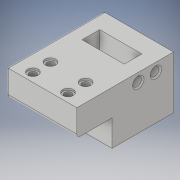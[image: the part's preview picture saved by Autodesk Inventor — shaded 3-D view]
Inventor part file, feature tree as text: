
AUTODESK INVENTOR PART (.ipt)
format: ipt  version: 2019 (Build 230136000, 136)  size: 223,744 bytes
history: native  units: mm
features: sketch x10, extrude x5, hole x5, fillet x2, mirror x1
ambient origin geometry x8: Origin, YZ Plane, XZ Plane, XY Plane, X Axis, Y Axis, Z Axis, Center Point
bodies: Solid1 (feature_tree)
feature tree (23):
  extrude  "Extrusion1"  Depth=20.0mm
  hole  "Hole1"  [1 undecoded]
  fillet  "Fillet1"  Radius=2.0mm
  extrude  "Extrusion2"  Depth=30.0mm
  extrude  "Extrusion3"  Depth=10.0mm TaperAngle=0.0deg
  hole  "Hole2"  [1 undecoded]
  hole  "Hole3"  [1 undecoded]
  extrude  "Extrusion4"  Depth=10.0mm
  extrude  "Extrusion5"  Depth=20.0mm
  hole  "Hole4"  [1 undecoded]
  hole  "Hole5"  [1 undecoded]
  mirror  "Mirror1"
  fillet  "Fillet2"  Radius=0.75mm
  sketch  "Sketch1"  dims[d0=40.0mm d1=20.0mm]
  sketch  "Sketch2"  dims[d2=15.0mm d3=0.0mm d4=20.0mm]
  sketch  "Sketch3"  dims[d5=4.0mm d6=6.0mm d7=6.0mm d8=1.0mm d9=90.0deg d10=8.0mm d11=20.594885mm d12=2.0mm]
  sketch  "Sketch4"  dims[d13=5.0mm d14=30.0mm]
  sketch  "Sketch5"  dims[d15=15.0mm d16=0.0mm d17=10.0mm d18=0.0mm]
  sketch  "Sketch6"  dims[d19=7.5mm d20=6.0mm d21=8.4mm d22=2.3mm d23=90.0deg d24=10.0mm d25=0.0mm]
  sketch  "Sketch7"  dims[d26=19.2mm d27=6.0mm d28=8.4mm d29=2.3mm d30=90.0deg d31=6.5mm d32=0.0mm d33=8.0mm]
  sketch  "Sketch8"  dims[d34=10.0mm d35=0.0mm d36=10.0mm d37=0.0mm]
  sketch  "Sketch9"  dims[d38=7.5mm d39=6.0mm d40=19.2mm d41=6.0mm d42=90.0deg d43=6.5mm d44=0.0mm d45=10.0mm]
  sketch  "Sketch10"  dims[d46=5.0mm d47=20.0mm d48=5.0mm d49=6.0mm d50=6.5mm d51=6.0mm d52=90.0deg d53=6.0mm d54=20.594885mm d55=1.0mm d56=1.0mm d57=6.0mm d58=6.5mm d59=5.0mm d60=5.0mm d61=14.3117mm d62=0.75mm d63=20.594885mm d64=0.0625mm d65=0.75mm d66=0.375mm]
note: 5 required parameter values undecoded (feature->parameter linkage not recoverable at this tier; creation-order binding heuristic only, values carry confidence <= 0.55)
